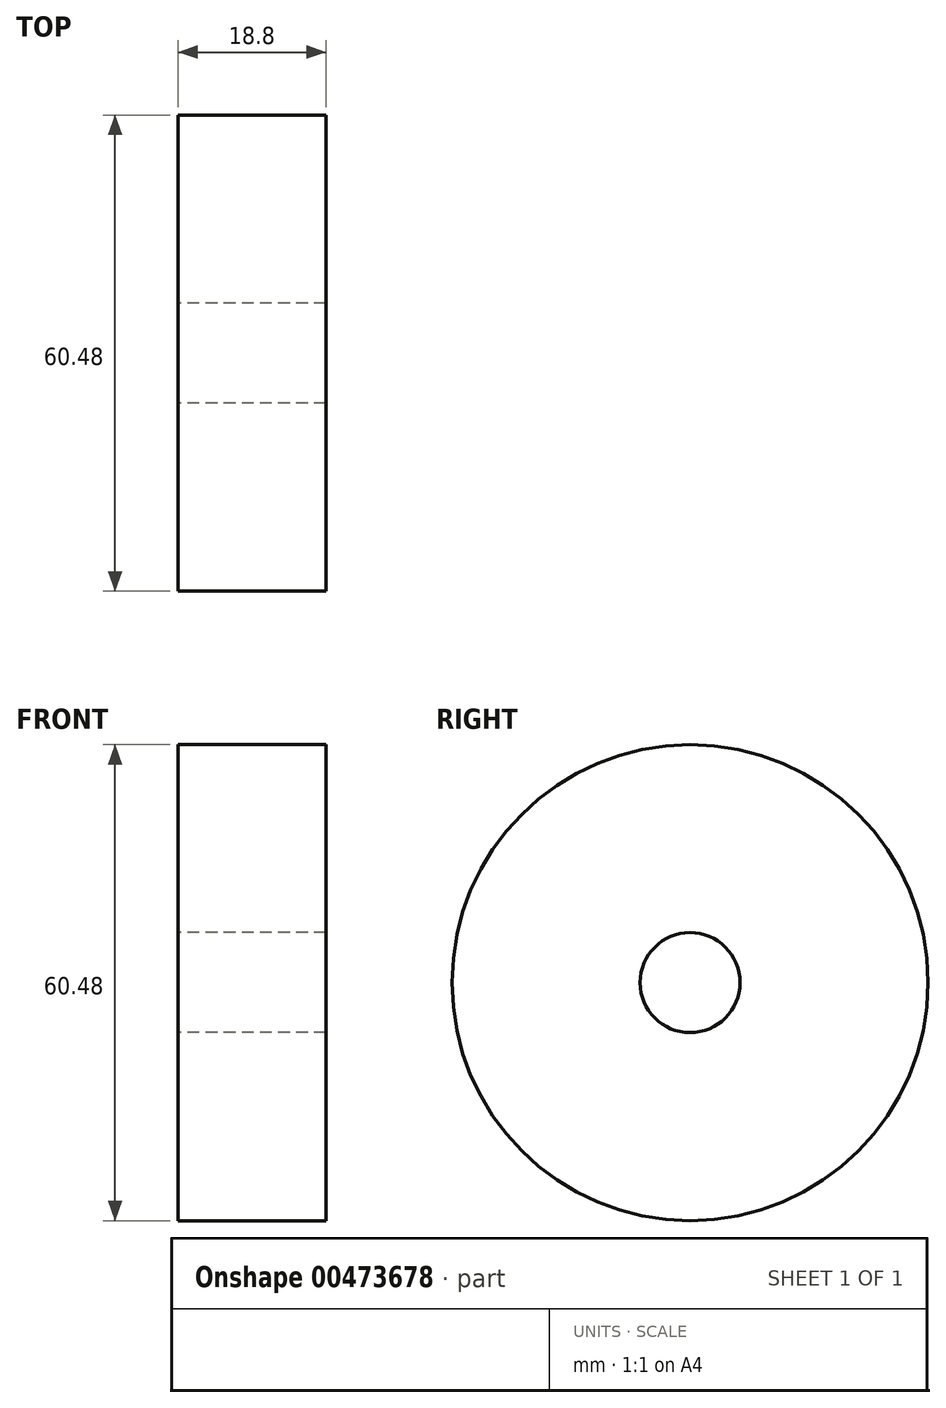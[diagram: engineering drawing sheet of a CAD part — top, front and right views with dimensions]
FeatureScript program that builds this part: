
annotation { "Feature Type Name" : "Feature", "Feature Type Description" : "" }
export const myFeature = defineFeature(function(context is Context, id is Id, definition is map)
    precondition{}
    {
        {
            var Q0;
            Q0=qCreatedBy(makeId("Right.planeOp"),FACE);
            var sketch = newSketch(context, id + "F0", { "sketchPlane" : qUnion([Q0])});
            skCircle(sketch, "E0", {"center": v(0, 0) * mm, "radius": 6.35 * mm});
            skCircle(sketch, "E1", {"center": v(0, 0) * mm, "radius": 30.24 * mm});
            skSolve(sketch);
        }
        {
            var Q0;
            Q0 = qSketchRegion(id + "F0", true);
            var Q1;
            Q1=makeQuery(id+"F0.imprint","IMPRINT",FACE,{"disambiguationData":[TD([[makeQuery(id+"F0.imprint","IMPRINT",EDGE,{"derivedFrom":sQuery(id+"F0.wireOp",EDGE,"E0")}),-1.0]])]});
            extrude(context, id + "F1", {"entities" : qUnion([Q0, Q1]), "depth" : 18.8 * mm, "offsetDistance" : 25.4 * mm});
        }
    });
